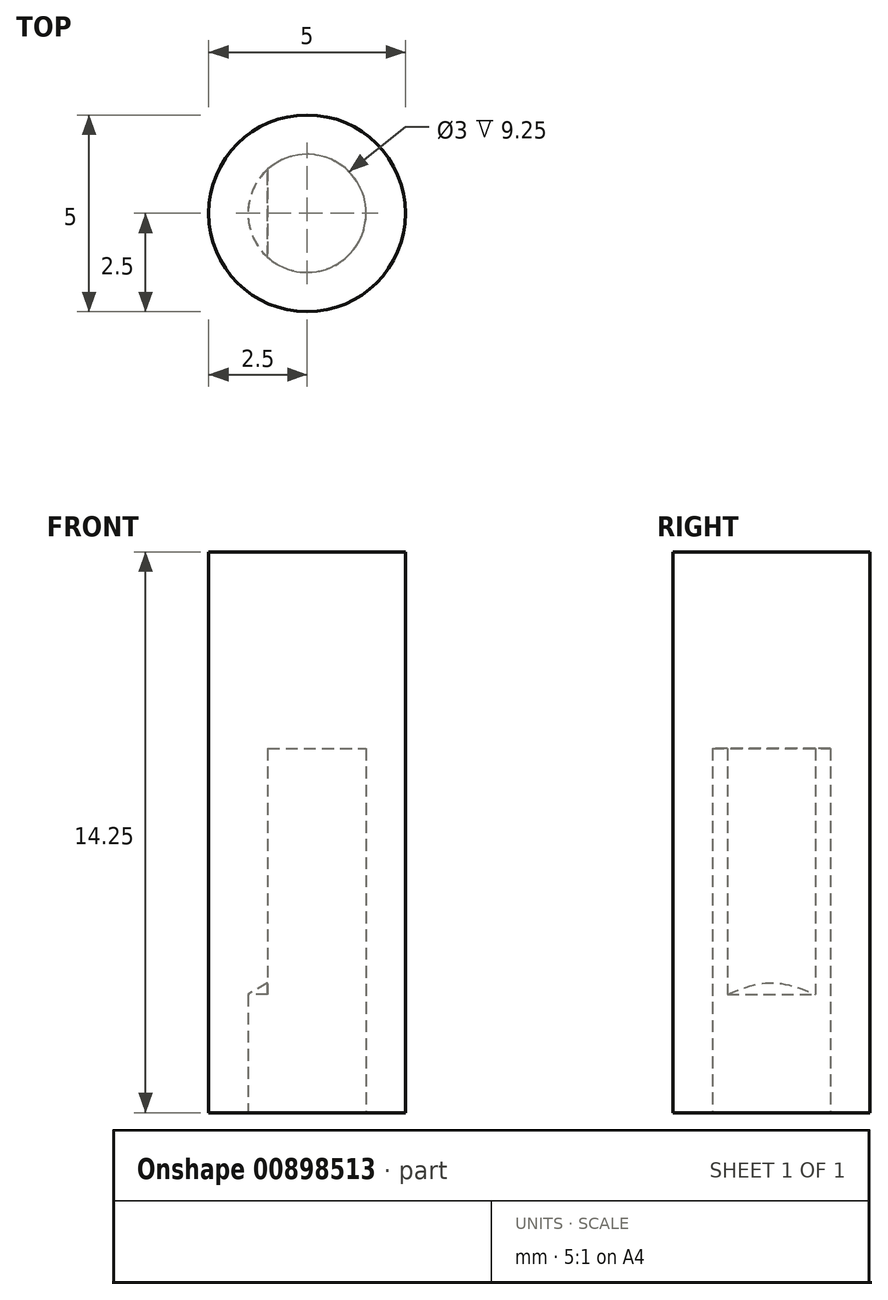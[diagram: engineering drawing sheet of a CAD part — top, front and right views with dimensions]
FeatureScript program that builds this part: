
annotation { "Feature Type Name" : "Feature", "Feature Type Description" : "" }
export const myFeature = defineFeature(function(context is Context, id is Id, definition is map)
    precondition{}
    {
        {
            var Q0;
            Q0=qCreatedBy(makeId("Top.planeOp"),FACE);
            var sketch = newSketch(context, id + "F0", { "sketchPlane" : qUnion([Q0])});
            skCircle(sketch, "E0", {"center": v(0, 0) * mm, "radius": 2.5 * mm});
            skArc(sketch, "E1", {"start": v(-1, -1.12) * mm, "mid": v(1.5, 0) * mm, "end": v(-1, 1.12) * mm});
            skLineSegment(sketch, "E2", {"start": v(-1, 1.12) * mm, "end": v(-1, -1.12) * mm});
            skSolve(sketch);
        }
        {
            var Q0;
            Q0 = qSketchRegion(id + "F0", true);
            extrude(context, id + "F1", {"entities" : qUnion([Q0]), "depth" : 14.25 * mm, "offsetDistance" : 25 * mm});
        }
        {
            var Q0;
            Q0=makeQuery(id+"F1.opExtrude","CAP_FACE",FACE,{"disambiguationData":[OSD([sQuery(id+"F0.wireOp",EDGE,"E0"),sQuery(id+"F0.wireOp",EDGE,"E1"),sQuery(id+"F0.wireOp",EDGE,"E2")])],"isStart":true});
            var sketch = newSketch(context, id + "F2", { "sketchPlane" : qUnion([Q0])});
            skPoint(sketch, "E3", {"position": v(0, 0) * mm});
            skSolve(sketch);
        }
        {
            var Q0;
            Q0=sQuery(id+"F2.wireOp",VERTEX,"E3");
            var Q1;
            Q1=makeQuery(id+"F1.opExtrude","SWEPT_BODY",BODY,{"disambiguationData":[OSD([sQuery(id+"F0.wireOp",EDGE,"E0"),sQuery(id+"F0.wireOp",EDGE,"E1"),sQuery(id+"F0.wireOp",EDGE,"E2")])]});
            hole(context, id + "F3", {"style" : HoleStyle.SIMPLE, "endStyle" : HoleEndStyle.BLIND, "holeDiameter" : 3 * mm, "majorDiameter" : 6.35 * mm, "holeDepth" : 3 * mm, "isTappedThrough" : true, "tappedDepth" : 12 * mm, "tapClearance" : 3, "locations" : qUnion([Q0]), "scope" : qUnion([Q1])});
        }
        {
            var Q0;
            Q0=makeQuery(id+"F1.opExtrude","CAP_FACE",FACE,{"disambiguationData":[OSD([sQuery(id+"F0.wireOp",EDGE,"E0"),sQuery(id+"F0.wireOp",EDGE,"E1"),sQuery(id+"F0.wireOp",EDGE,"E2")])],"isStart":false});
            var sketch = newSketch(context, id + "F4", { "sketchPlane" : qUnion([Q0])});
            skCircle(sketch, "E4", {"center": v(0, 0) * mm, "radius": 2.15 * mm});
            skSolve(sketch);
        }
        {
            var Q0;
            Q0=makeQuery(id+"F4.imprint","IMPRINT",FACE,{"disambiguationData":[TD([[makeQuery(id+"F4.imprint","IMPRINT",EDGE,{"derivedFrom":sQuery(id+"F4.wireOp",EDGE,"E4")}),1.0]])]});
            var Q1;
            Q1=makeQuery(id+"F4.imprint","IMPRINT",FACE,{"disambiguationData":[TD([[makeQuery(id+"F4.imprint","IMPRINT",EDGE,{"derivedFrom":makeQuery(id+"F1.opExtrude","CAP_EDGE",EDGE,{"disambiguationData":[OSD([sQuery(id+"F0.wireOp",EDGE,"E1")])],"isStart":false})}),1.0]])]});
            var Q2;
            Q2=sQuery(id+"F4.wireOp",EDGE,"E4");
            extrude(context, id + "F5", {"entities" : qUnion([Q0, Q1]), "operationType" : NewBodyOperationType.ADD, "surfaceOperationType" : NewSurfaceOperationType.ADD, "surfaceEntities" : qUnion([Q2]), "oppositeDirection" : true, "depth" : 5 * mm, "offsetDistance" : 25 * mm});
        }
    });
